# Revit family: Display-LCD-Panasonic-AF1Series
name_source: partatom
category: Communication Devices
revit_build: Autodesk Revit 2013 (Build: 20130531_2115(x64)
units: mm (PartAtom-declared; Revit-internal decimal feet)

## types (3) — shared parameters
Aspect Ratio = 16:9
Audio In = Stereo mini jack (M3) x1(Shared with VIDEO IN, COMPONENT IN, PC IN, DVI-D IN)
Audio Out = Stereo mini jack (M3) x1
Component RGB In = BNC x1
DVI D In = DVI-D 24pin x1
DVI D Out = DVI-D 24pin x1
Date Last Modified = 2016/6/30
Default Elevation = 1219.2 mm  [stored 4 ft]
Depth = 72 mm  [stored 0.23622 ft]
Equipment Abbreviation = PTV
Family Version = 1.0.0
HDMI In = HDMI Type A Connector x2
LAN = RJ45 x1
Manufacturer = Panasonic
Model Disclaimer = Contact Panasonic for more information
PC In = Mini D-sub 15pin x1
Panel Type = IPS / Edge-LED
Power Standby = 0.5 W
Product Documentation Link = http://www.panasonic.net
Product Material = Plastic - Panasonic - Black
Product Page URL = http://www.panasonic.net
Provide Feedback = https://www.surveymonkey.com
Regulatory Compliance = UL60950-1 2nd Edition, CAN/CSA-C22.2 No. 60950-1-07 FCC47 CFR, Part 15, Subpart B Class A, ICES-003
Serial = D-sub 9pin x1(Serial In)
URL = http://panasonic.net
Video In = BNC x1
Voltage AC = 110 V
zz Length Frame Depth = -57 mm  [stored -0.187008 ft]
zz Length Pede Depth = 330 mm
zz Length Pede Top Height = 127 mm  [stored 0.416667 ft]
zz Length Thick Bottom = 6.3 mm  [stored 0.0206693 ft]
zz Length Thick Side = 6.3 mm  [stored 0.0206693 ft]
zz Length Thick Top = 6.3 mm  [stored 0.0206693 ft]
zero-valued in all types: zz Pos Base Depth

## per-type parameters (varying)
| type | Description | Height | Model | Part Description | Part Number | Power Active | Power Peak | Weight | Width | zz Integer 1 | zz Length Inner Height | zz Length Inner Width | zz Length Pede Back Height | zz Length Pede Height | zz Length Pede Width | zz Pos Pede Back Side | zz Pos Pede Side | zz Pos Pede Tail |
| 42", 1080p Full HD LCD Display, 500cd, TH-42AF1U | 42" LCD Display, Full HD, 500cd | 541 mm  [stored 1.77493 ft] | TH-42AF1U | 42" LCD Display, Full HD, 500cd | TH-42AF1U | 110.0 W | 155.0 W | 34.40 lb | 947 mm  [stored 3.10696 ft] | 1 | 528.4 mm  [stored 1.7336 ft] | 934.4 mm | 80 mm  [stored 0.262467 ft] | 47 mm  [stored 0.154199 ft] | 75.5 mm  [stored 0.247703 ft] | 22.75 mm  [stored 0.0746391 ft] | 363 mm  [stored 1.19094 ft] | 106 mm  [stored 0.347769 ft] |
| 49", 1080p Full HD LCD Display, 500cd, TH-49AF1U | 49" LCD Display, Full HD, 500cd | 623 mm  [stored 2.04396 ft] | TH-49AF1U | 49" LCD Display, Full HD, 500cd | TH-49AF1U | 130.0 W | 175.0 W | 42.60 lb | 1093 mm  [stored 3.58596 ft] | 3 | 610.4 mm | 1080.4 mm  [stored 3.54462 ft] | 75 mm | 52 mm | 75.5 mm  [stored 0.247703 ft] | 22.75 mm  [stored 0.0746391 ft] | 371 mm  [stored 1.21719 ft] | 107 mm  [stored 0.35105 ft] |
| 55", 1080p Full HD LCD Display, 500cd, TH-55AF1U | 55" LCD Display, Full HD, 500cd | 699 mm  [stored 2.29331 ft] | TH-55AF1U | 55" LCD Display, Full HD, 500cd | TH-55AF1U | 145.0 W | 190.0 W | 55.20 lb | 1229 mm  [stored 4.03215 ft] | 5 | 686.4 mm | 1216.4 mm | 91 mm  [stored 0.298556 ft] | 36 mm  [stored 0.11811 ft] | 76 mm  [stored 0.249344 ft] | 23 mm  [stored 0.0754593 ft] | 344.5 mm  [stored 1.13025 ft] | 107 mm  [stored 0.35105 ft] |

note: [stored X ft] marks values corroborated as IEEE doubles in the binary element streams (Revit-internal decimal feet)

## geometry (parser evidence)
native form markers: Blend x18, Extrusion x2, Sweep x2
no freeform markers — native parametric forms only
